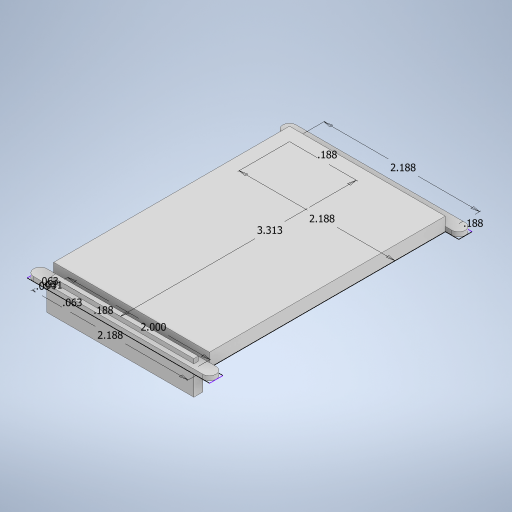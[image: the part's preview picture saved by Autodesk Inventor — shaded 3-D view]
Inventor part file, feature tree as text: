
AUTODESK INVENTOR PART (.ipt)
format: ipt  version: 2023 (Build 270158000, 158)  size: 284,672 bytes
history: native  units: in
note: dims shown in document units (in); Inventor stores cm internally (conversion verified against a paired STEP export)
features: extrude x5, sketch x1, fillet x1
ambient origin geometry x8: Origin, YZ Plane, XZ Plane, XY Plane, X Axis, Y Axis, Z Axis, Center Point
bodies: Solid1 (feature_tree)
feature tree (7):
  sketch  "Sketch1"  dims[d0=2.1875in d1=3.3125in d2=2.1875in d4=2.1875in d7=0.1875in d8=0.1875in d9=0.1875in d10=2.0in d12=0.0625in d13=0.0625in d14=0.0938in d15=0.0312in d16=0.1875in d17=0.0in d18=0.0625in d19=0.0in d20=0.0625in d21=0.0in d22=0.125in d23=0.0in d24=0.3125in d25=0.0in d26=0.0938in]
  extrude  "Extrusion1"  Depth=3.3125in
  extrude  "Extrusion2"  Depth=2.1875in
  extrude  "Extrusion3"  Depth=2.1875in
  extrude  "Extrusion4"  Depth=0.1875in
  extrude  "Extrusion5"  Depth=0.1875in
  fillet  "Fillet1"  Radius=0.1875in
